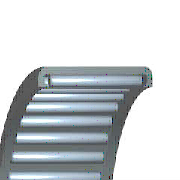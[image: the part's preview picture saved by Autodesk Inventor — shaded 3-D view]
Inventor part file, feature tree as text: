
AUTODESK INVENTOR PART (.ipt)
format: ipt  version: 2016 (Build 200138000, 138)  size: 293,888 bytes
history: native  units: mm (DEFAULTED — no unit token found)
features: sketch x1, other x1, pattern_circular x1
ambient origin geometry x8: Origin, YZ Plane, XZ Plane, XY Plane, X Axis, Y Axis, Z Axis, Center Point
bodies: Solid1 (feature_tree), Body (feature_tree)
feature tree (3):
  sketch  "Sketch"  dims[d36=90.0deg d0=1.25mm d1=0.25mm d39=90.0deg d2=200.0mm d3=360.0deg d4=0.0mm d5=0.0mm d6=1.4mm d7=0.0mm d8=12.0mm d9=16.0mm d10=13.0mm d11=14.0mm d12=1.0mm d13=1.9mm d14=7.0mm d57=0.0mm d58=0.0mm]
  other  "Roller"
  pattern_circular  "Rollers"  [2 undecoded]
note: 2 required parameter values undecoded (feature->parameter linkage not recoverable at this tier; creation-order binding heuristic only, values carry confidence <= 0.55)
